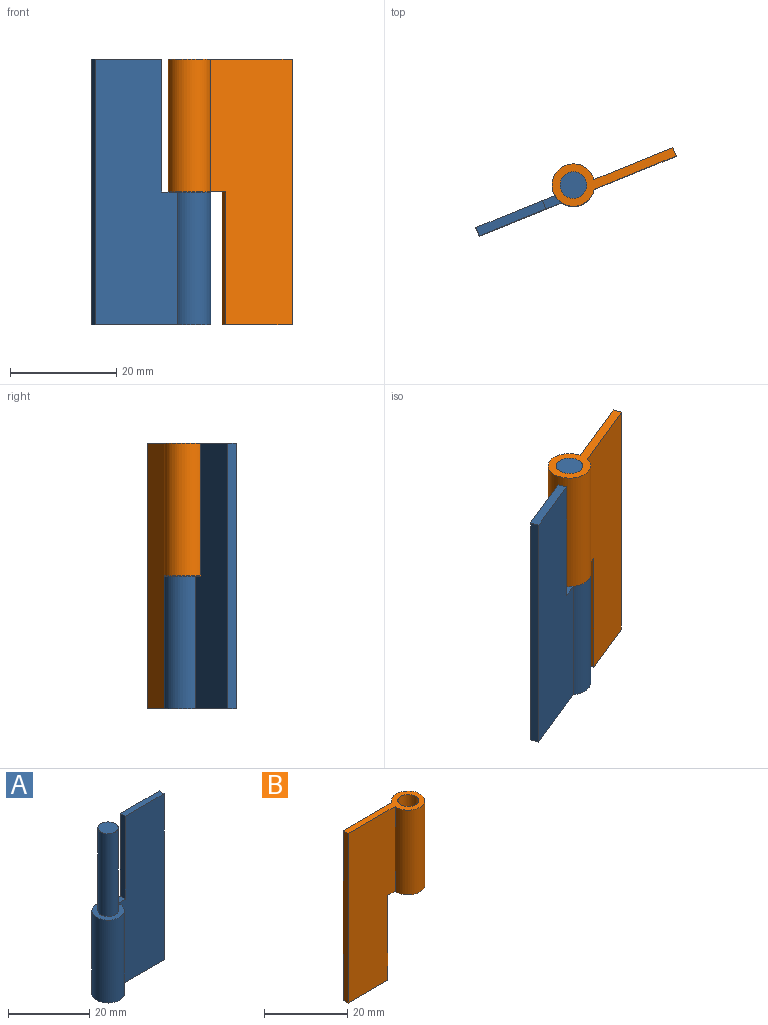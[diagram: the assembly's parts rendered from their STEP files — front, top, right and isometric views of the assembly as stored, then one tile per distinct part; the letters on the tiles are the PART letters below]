
ASSEMBLY  parts=2 mates=1
PART A: 10 faces, bbox 24x8x50 mm
  f0: plane 24x8mm, normal (0,0,-1), area 77.9mm2, adj f1,f3,f4,f5
  f1: cylinder r=4mm len=25mm, axis (0,0,1), area 582.6mm2, adj f0,f2,f3,f4
  f2: plane 10.5x8mm, normal (0,0,1), area 35.3mm2, adj f1,f3,f4,f6,f9
  f3: plane 50x16.66mm, normal (0,1,0), area 754mm2, adj f0,f1,f2,f5,f8,f9
  f4: plane 50x16.03mm, normal (0,-1,0), area 738.3mm2, adj f0,f1,f2,f5,f8,f9
  f5: plane 50x1.7mm, normal (1,0,0), area 85mm2, adj f0,f3,f4,f8
  f6: cylinder r=2.5mm len=25mm, axis (0,0,-1), area 392.7mm2, adj f2,f7
  f7: plane 5x5mm, normal (0,0,1), area 19.6mm2, adj f6
  f8: plane 13.5x1.7mm, normal (0,0,1), area 23mm2, adj f3,f4,f5,f9
  f9: plane 25x1.7mm, normal (-1,0,0), area 42.5mm2, adj f2,f3,f4,f8
PART B: 9 faces, bbox 24x8x50 mm
  f0: plane 50x16mm, normal (0,-1,0), area 737.5mm2, adj f1,f3,f5,f6,f7,f8
  f1: cylinder r=4mm len=25mm, axis (0,0,-1), area 582.6mm2, adj f0,f2,f5,f6
  f2: plane 50x16.63mm, normal (0,1,0), area 753.2mm2, adj f1,f3,f5,f6,f7,f8
  f3: plane 50x1.7mm, normal (-1,0,0), area 85mm2, adj f0,f2,f5,f8
  f4: cylinder r=2.5mm len=25mm, axis (0,0,-1), area 392.7mm2, adj f5,f6
  f5: plane 23.97x8mm, normal (0,0,1), area 58.2mm2, adj f0,f1,f2,f3,f4
  f6: plane 10.47x8mm, normal (0,0,-1), area 35.3mm2, adj f0,f1,f2,f4,f7
  f7: plane 25x1.7mm, normal (1,0,0), area 42.5mm2, adj f0,f2,f6,f8
  f8: plane 13.5x1.7mm, normal (0,0,-1), area 23mm2, adj f0,f2,f3,f7
PLACE A rot(axis=(0,0,-1),157.9deg) t=(-12.23,-2.12,8.76)mm fixed
PLACE B rot(axis=(0,0,-1),157.9deg) t=(-12.23,-2.12,8.76)mm
MATE revolute A.f6 <-> B.f4  axis (0,0,1) through (-12.23,-2.12,33.76)mm
